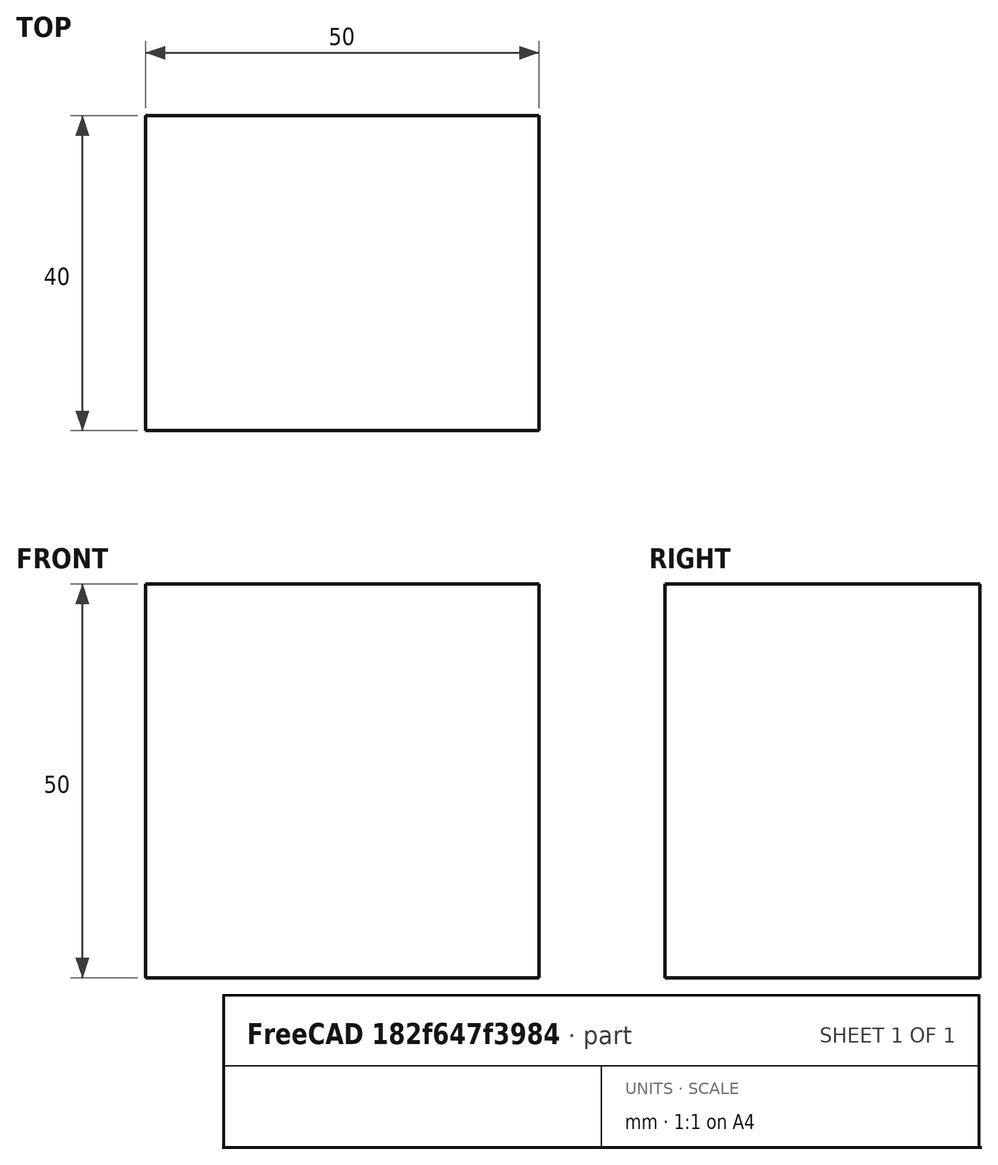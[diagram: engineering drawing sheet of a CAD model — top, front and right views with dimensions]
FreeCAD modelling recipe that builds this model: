
FCSTD DOCUMENT  (FreeCAD 0.15R4671 (Git))
Label: Flat Bar 50x40 EN10058 S235JR
License: All rights reserved
LicenseURL: http://en.wikipedia.org/wiki/All_rights_reserved
objects: Sketcher::SketchObject×1, Part::Extrusion×1
note: 2 computed .brp shape members not serialized (recipe doc carries the construction recipe); baked Part::Feature solids carry a one-line shape summary decoded from their .brp

FEATURE [Sketcher::SketchObject] Sketch
  sketch-geometry (4):
    g0: LineSegment StartX=-25 StartY=-20 StartZ=0 EndX=25 EndY=-20 EndZ=0
    g1: LineSegment StartX=25 StartY=-20 StartZ=0 EndX=25 EndY=20 EndZ=0
    g2: LineSegment StartX=25 StartY=20 StartZ=0 EndX=-25 EndY=20 EndZ=0
    g3: LineSegment StartX=-25 StartY=20 StartZ=0 EndX=-25 EndY=-20 EndZ=0
  constraints (12):
    c: Coincident(g0,g1)
    c: Coincident(g1,g2)
    c: Coincident(g2,g3)
    c: Coincident(g3,g0)
    c: Horizontal(g0)
    c: Horizontal(g2)
    c: Vertical(g1)
    c: Vertical(g3)
    c: Symmetric(g1,g2,g-2)
    c: Symmetric(g0,g1,g-1)
    c: DistanceY(g1) = 40
    c: DistanceX(g0) = 50
FEATURE [Part::Extrusion] Extrude  label="Flat Bar 50x40 EN10058 S235JR"
  Base = -> Sketch
  Dir = (0,0,50)
  Solid = true
